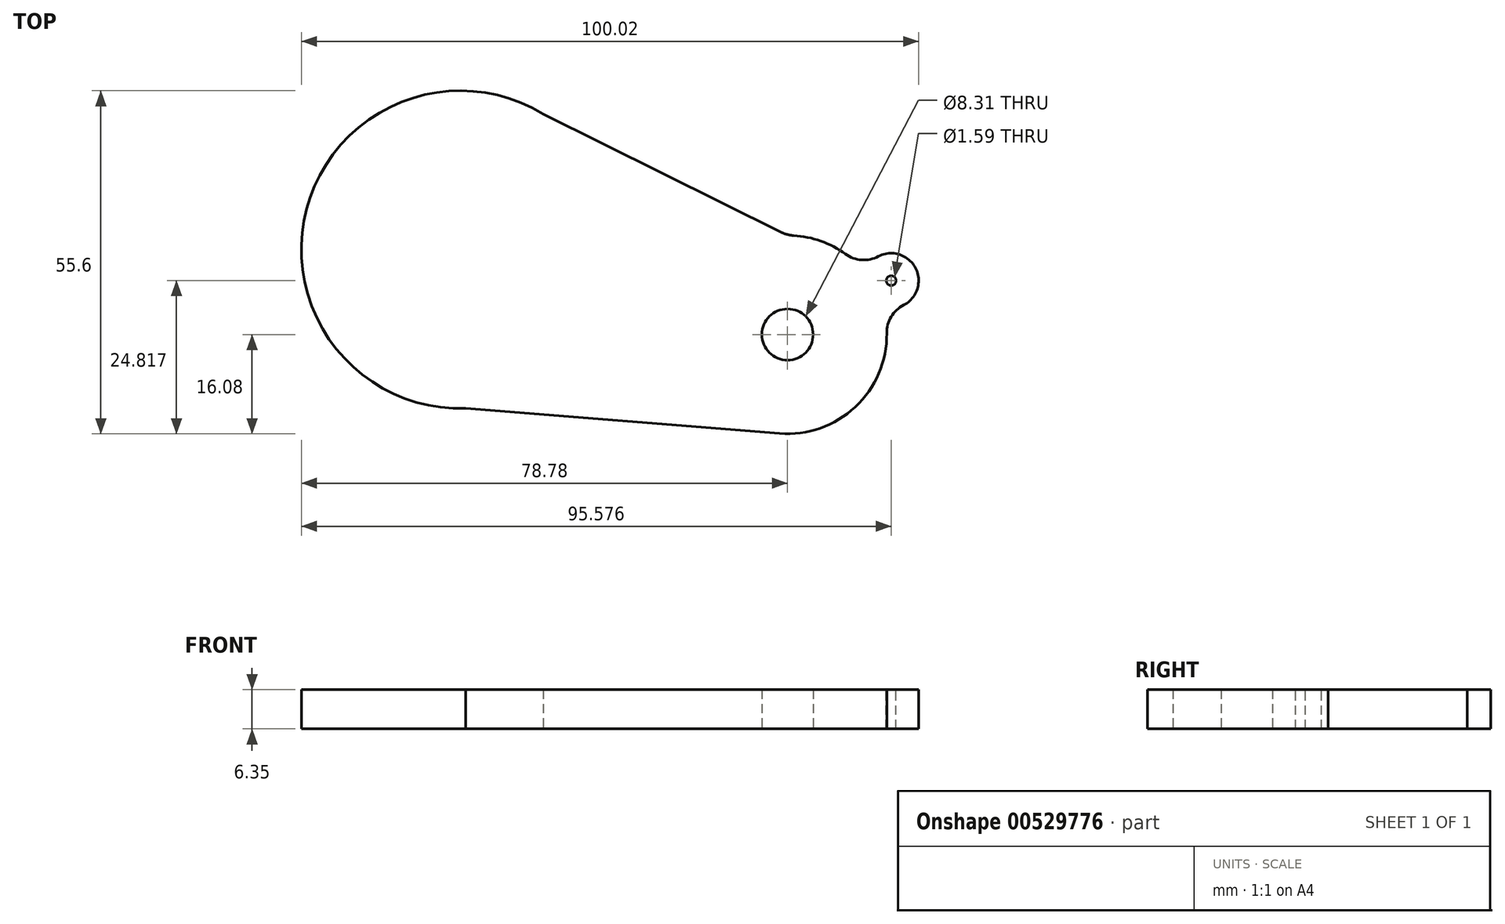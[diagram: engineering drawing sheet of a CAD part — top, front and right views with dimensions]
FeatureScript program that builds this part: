
annotation { "Feature Type Name" : "Feature", "Feature Type Description" : "" }
export const myFeature = defineFeature(function(context is Context, id is Id, definition is map)
    precondition{}
    {
        {
            var Q0;
            Q0=qCreatedBy(makeId("Top.planeOp"),FACE);
            var sketch = newSketch(context, id + "F0", { "sketchPlane" : qUnion([Q0])});
            skCircle(sketch, "E0", {"center": v(-53.03, 13.77) * mm, "radius": 25.75 * mm});
            skCircle(sketch, "E1", {"center": v(0, 0) * mm, "radius": 16.08 * mm});
            skCircle(sketch, "E2", {"center": v(0, 0) * mm, "radius": 4.15 * mm});
            skLineSegment(sketch, "E3", {"start": v(-57.96, -11.5) * mm, "end": v(0, -16.13) * mm});
            skLineSegment(sketch, "E4", {"start": v(0, 16.08) * mm, "end": v(-43.66, 37.76) * mm});
            skCircle(sketch, "E5", {"center": v(16.8, 8.74) * mm, "radius": 4.45 * mm});
            skSolve(sketch);
        }
        {
            var Q0;
            Q0 = qSketchRegion(id + "F0", true);
            extrude(context, id + "F1", {"entities" : qUnion([Q0]), "depth" : 6.35 * mm, "offsetDistance" : 25.4 * mm});
        }
        {
            var Q0;
            {var subQ0=sQuery(id+"F0.wireOp",EDGE,"E5");var subQ1=sQuery(id+"F0.wireOp",EDGE,"E1");Q0=makeQuery(id+"F1.opExtrude","SWEPT_EDGE",EDGE,{"disambiguationData":[OSD([subQ1,subQ0]),TDD([makeQuery(id+"F0.imprint","INTERSECT",VERTEX,{"disambiguationData":[OD(1.0)],"derivedFrom":[subQ1,subQ0]})])]});}
            var Q1;
            {var subQ0=sQuery(id+"F0.wireOp",EDGE,"E5");var subQ1=sQuery(id+"F0.wireOp",EDGE,"E1");Q1=makeQuery(id+"F1.opExtrude","SWEPT_EDGE",EDGE,{"disambiguationData":[OSD([subQ1,subQ0]),TDD([makeQuery(id+"F0.imprint","INTERSECT",VERTEX,{"disambiguationData":[OD(0.0)],"derivedFrom":[subQ1,subQ0]})])]});}
            var Q2;
            Q2=makeQuery(id+"F1.opExtrude","SWEPT_EDGE",EDGE,{"disambiguationData":[OSD([sQuery(id+"F0.wireOp",EDGE,"E1"),sQuery(id+"F0.wireOp",EDGE,"E4")])]});
            fillet(context, id + "F2", {"entities" : qUnion([Q0, Q1, Q2]), "radius" : 5.08 * mm, "tangentPropagation" : true, "allowEdgeOverflow" : false});
        }
        {
            var Q0;
            Q0=makeQuery(id+"F1.opExtrude","CAP_FACE",FACE,{"disambiguationData":[OSD([sQuery(id+"F0.wireOp",EDGE,"E0"),sQuery(id+"F0.wireOp",EDGE,"E1"),sQuery(id+"F0.wireOp",EDGE,"E2"),sQuery(id+"F0.wireOp",EDGE,"E3"),sQuery(id+"F0.wireOp",EDGE,"E4"),sQuery(id+"F0.wireOp",EDGE,"E5")])],"isStart":false});
            var sketch = newSketch(context, id + "F3", { "sketchPlane" : qUnion([Q0])});
            skCircle(sketch, "E6", {"center": v(16.8, 8.74) * mm, "radius": 0.8 * mm});
            skSolve(sketch);
        }
        {
            var Q0;
            Q0 = qSketchRegion(id + "F3", true);
            extrude(context, id + "F4", {"entities" : qUnion([Q0]), "operationType" : NewBodyOperationType.REMOVE, "oppositeDirection" : true, "depth" : 6.6 * mm, "offsetDistance" : 25.4 * mm});
        }
    });
